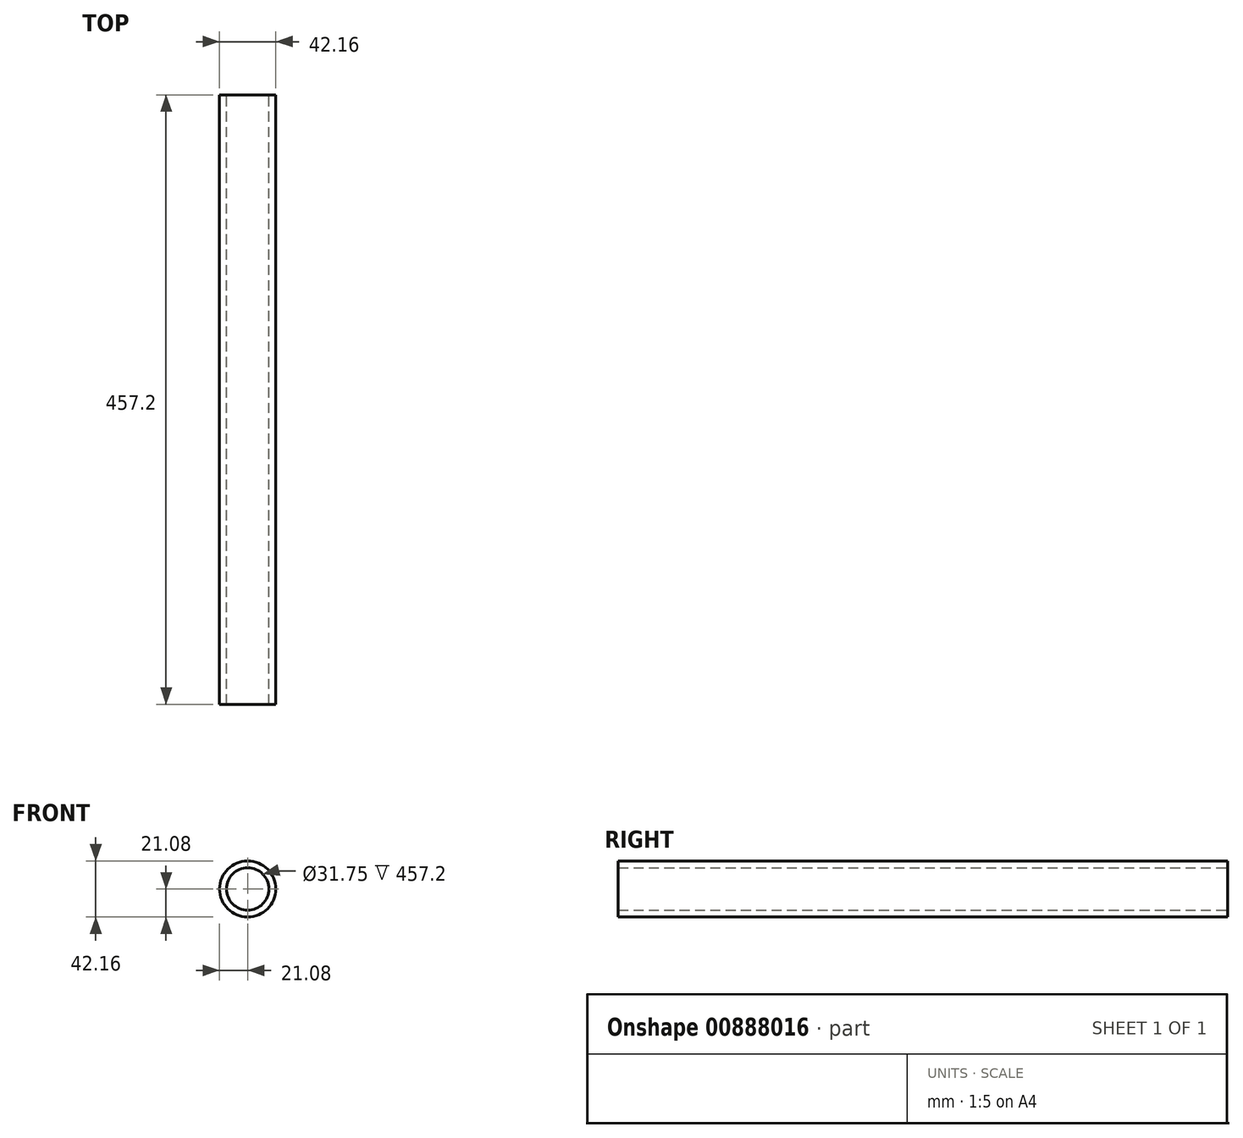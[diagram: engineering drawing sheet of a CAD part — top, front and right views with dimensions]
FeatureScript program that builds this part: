
annotation { "Feature Type Name" : "Feature", "Feature Type Description" : "" }
export const myFeature = defineFeature(function(context is Context, id is Id, definition is map)
    precondition{}
    {
        {
            var Q0;
            Q0=qCreatedBy(makeId("Front.planeOp"),FACE);
            var sketch = newSketch(context, id + "F0", { "sketchPlane" : qUnion([Q0])});
            skCircle(sketch, "E0", {"center": v(0, 0) * mm, "radius": 15.88 * mm});
            skCircle(sketch, "E1", {"center": v(0, 0) * mm, "radius": 21.08 * mm});
            skSolve(sketch);
        }
        {
            var Q0;
            Q0=makeQuery(id+"F0.imprint","IMPRINT",FACE,{"disambiguationData":[TD([[makeQuery(id+"F0.imprint","IMPRINT",EDGE,{"derivedFrom":sQuery(id+"F0.wireOp",EDGE,"E0")}),-1.0]])]});
            extrude(context, id + "F1", {"entities" : qUnion([Q0]), "depth" : 457.2 * mm, "offsetDistance" : 25.4 * mm});
        }
    });
